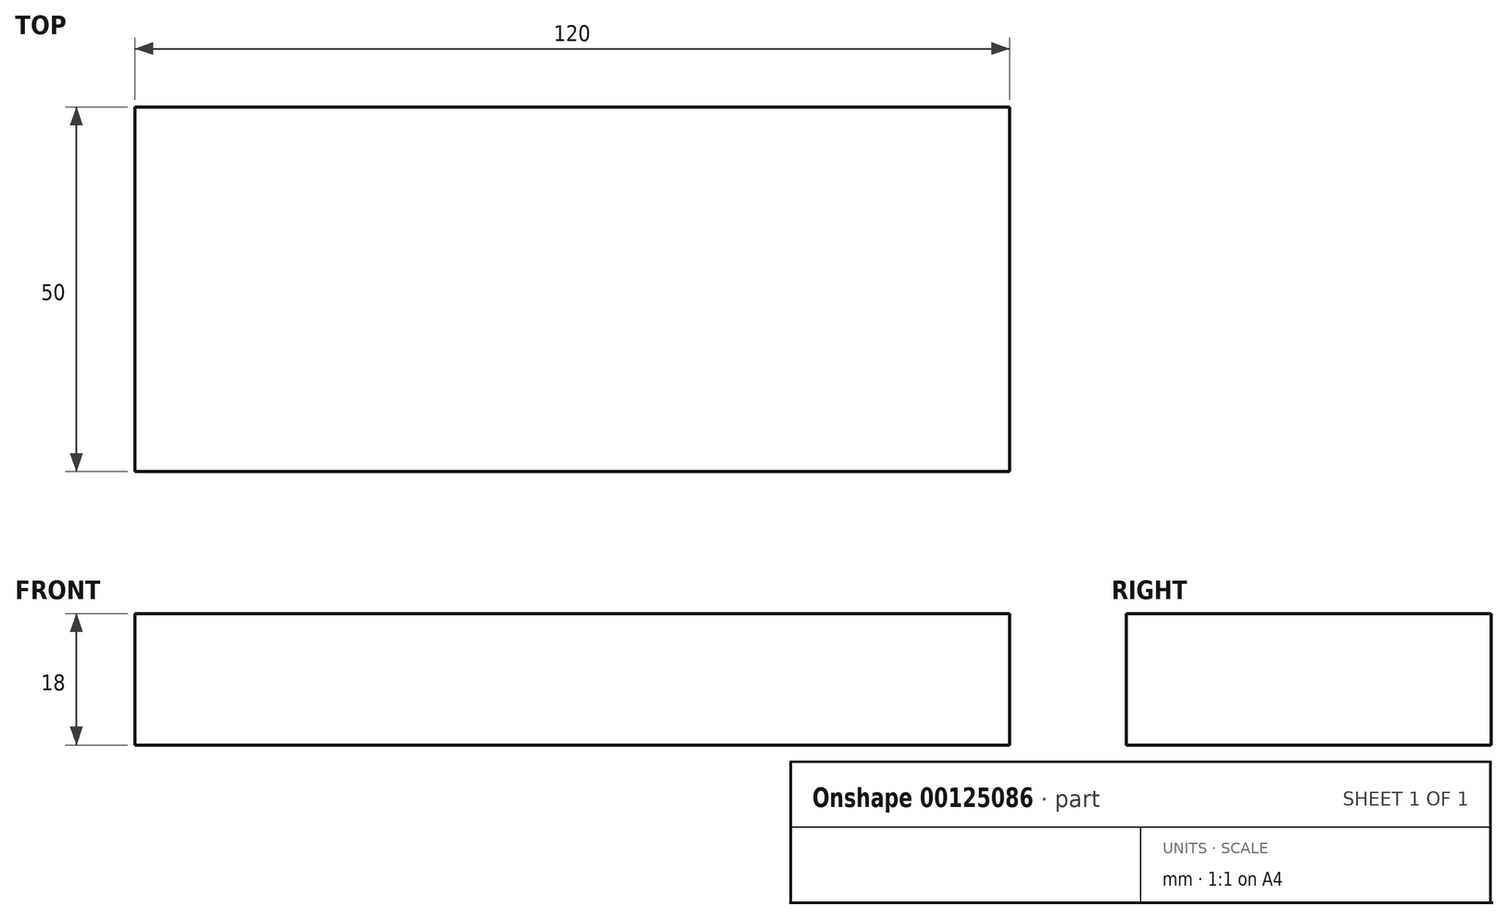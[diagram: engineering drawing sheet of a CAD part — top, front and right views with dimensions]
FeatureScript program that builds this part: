
annotation { "Feature Type Name" : "Feature", "Feature Type Description" : "" }
export const myFeature = defineFeature(function(context is Context, id is Id, definition is map)
    precondition{}
    {
        {
            var Q0;
            Q0=qCreatedBy(makeId("Top.planeOp"),FACE);
            var sketch = newSketch(context, id + "F0", { "sketchPlane" : qUnion([Q0])});
            skLineSegment(sketch, "E0.bottom", {"start": v(60, -25) * mm, "end": v(-60, -25) * mm});
            skLineSegment(sketch, "E0.top", {"start": v(60, 25) * mm, "end": v(-60, 25) * mm});
            skLineSegment(sketch, "E0.left", {"start": v(60, -25) * mm, "end": v(60, 25) * mm});
            skLineSegment(sketch, "E0.right", {"start": v(-60, -25) * mm, "end": v(-60, 25) * mm});
            skPoint(sketch, "E0.middle", {"position": v(0, 0) * mm});
            skSolve(sketch);
        }
        {
            var Q0;
            Q0=makeQuery(id+"F0.imprint","IMPRINT",FACE,{"disambiguationData":[TD([[makeQuery(id+"F0.imprint","IMPRINT",EDGE,{"derivedFrom":sQuery(id+"F0.wireOp",EDGE,"E0.bottom")}),-1.0]])]});
            extrude(context, id + "F1", {"entities" : qUnion([Q0]), "depth" : 18 * mm});
        }
    });
